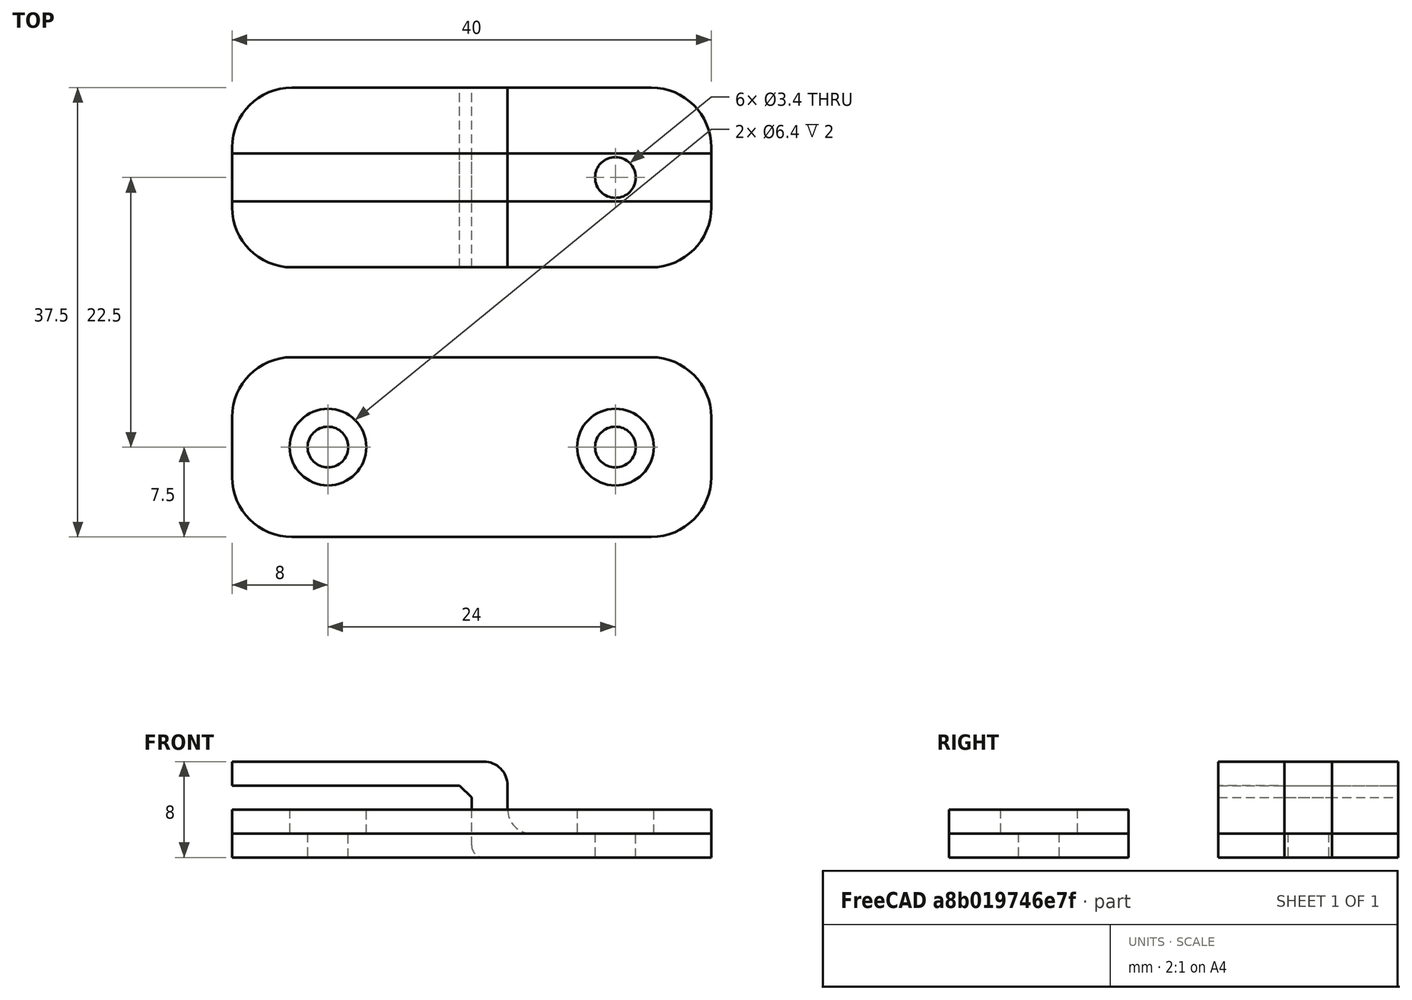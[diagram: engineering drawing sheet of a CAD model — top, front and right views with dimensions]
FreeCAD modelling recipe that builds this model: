
FCSTD DOCUMENT  (FreeCAD 0.20R29177 (Git))
Label: clamp_union_pedales
License: All rights reserved
LicenseURL: http://en.wikipedia.org/wiki/All_rights_reserved
objects: Part::Cut×8, Part::Box×6, Part::Fillet×4, Part::Cylinder×4, Mesh::Feature×4, Part::Feature×3, Part::Chamfer×1, Sketcher::SketchObject×1, PartDesign::Hole×1, PartDesign::Body×1, Part::MultiFuse×1
note: 31 computed .brp shape members not serialized (recipe doc carries the construction recipe); baked Part::Feature solids carry a one-line shape summary decoded from their .brp

FEATURE [Part::Box] Box  label="Cube"
  AttacherType = Attacher::AttachEngine3D
  Height = 8
  Length = 40
  Width = 15
FEATURE [Part::Box] Box001  label="Cube001"
  AttacherType = Attacher::AttachEngine3D
  Height = 6
  Length = 20
  Width = 15
FEATURE [Part::Box] Box002  label="Cube002"
  AttacherType = Attacher::AttachEngine3D
  Height = 6
  Length = 20
  Placement = pos=(23,0,2) rot=(0,0,1;0rad)
  Width = 15
FEATURE [Part::Cut] Cut
  Base = -> Box
  Tool = -> Box002
FEATURE [Part::Cut] Cut001
  Base = -> Cut
  Tool = -> Box001
FEATURE [Part::Fillet] Fillet
  Base = -> Cut001
  Edges = 4 edges r=5: [Edge1,Edge3,Edge5,Edge14]
FEATURE [Part::Fillet] Fillet001
  Base = -> Fillet
  Edges = 2 edges r=2: [Edge9,Edge23]
FEATURE [Part::Chamfer] Chamfer
  Base = -> Fillet001
  Edges = 1 edges r=1: [Edge41]
FEATURE [Part::Fillet] Fillet002
  Base = -> Chamfer
  Edges = 1 edges r=1: [Edge13]
FEATURE [Sketcher::SketchObject] Sketch
  FullyConstrained = false
  MapMode = 5
  Placement = pos=(0,0,2) rot=(0,0,1;0rad)
  Support = -> [Fillet002]
  sketch-geometry (1):
    g0: Circle CenterX=32 CenterY=7.5 CenterZ=0 NormalX=0 NormalY=0 NormalZ=1 AngleXU=0 Radius=2.58429
  constraints (2):
    c: DistanceX(g0) = 32
    c: DistanceY(g-1,g0) = 7.5
FEATURE [PartDesign::Hole] Hole
  CustomThreadClearance = 0
  Depth = 87.7945
  DepthType = 1
  Diameter = 3.4
  DrillForDepth = false
  DrillPoint = 1
  DrillPointAngle = 118
  HoleCutCountersinkAngle = 90
  HoleCutCustomValues = false
  HoleCutDepth = 0
  HoleCutDiameter = 6.1
  HoleCutType = 0
  ModelThread = false
  Profile = -> Sketch
  Tapered = false
  TaperedAngle = 90
  ThreadClass = 0
  ThreadDepth = 87.7945
  ThreadDepthType = 0
  ThreadDirection = 0
  ThreadFit = 0
  ThreadSize = 9
  ThreadType = 1
  Threaded = false
  UseCustomThreadClearance = false
FEATURE [PartDesign::Body] Body  label="clamp"
  Group = -> [Sketch,Hole]
  Origin = -> Origin
  Tip = -> Hole
FEATURE [Part::Box] Box003  label="Cube003"
  AttacherType = Attacher::AttachEngine3D
  Height = 2
  Length = 40
  Width = 15
FEATURE [Part::Fillet] Fillet003
  Base = -> Box003
  Edges = 4 edges r=5: [Edge1,Edge3,Edge5,Edge7]
  Placement = pos=(0,-7.5,0) rot=(0,0,1;0rad)
FEATURE [Part::Cylinder] Cylinder
  Angle = 360
  AttacherType = Attacher::AttachEngine3D
  FirstAngle = 0
  Height = 10
  Placement = pos=(8,0,0) rot=(0,0,1;0rad)
  Radius = 1.7
  SecondAngle = 0
FEATURE [Part::Cylinder] Cylinder001
  Angle = 360
  AttacherType = Attacher::AttachEngine3D
  FirstAngle = 0
  Height = 10
  Placement = pos=(32,0,0) rot=(0,0,1;0rad)
  Radius = 1.7
  SecondAngle = 0
FEATURE [Part::Cut] Cut002
  Base = -> Fillet003
  Tool = -> Cylinder
FEATURE [Part::Cut] Cut003  label="union"
  Base = -> Cut002
  Placement = pos=(0,-15,0) rot=(0,0,1;0rad)
  Tool = -> Cylinder001
FEATURE [Part::Feature] Body001  label="test"
  shape: bbox 40 x 15 x 8 mm, 19 faces (baked)
FEATURE [Part::Box] Box004  label="Cube004"
  AttacherType = Attacher::AttachEngine3D
  Height = 10
  Length = 44
  Width = 5.5
FEATURE [Part::Box] Box005  label="Cube005"
  AttacherType = Attacher::AttachEngine3D
  Height = 10
  Length = 44
  Placement = pos=(0,9.5,0) rot=(0,0,1;0rad)
  Width = 5.5
FEATURE [Part::Cut] Cut004
  Base = -> Body001
  Tool = -> Box004
FEATURE [Part::Cut] Cut005  label="test_clamp"
  Base = -> Cut004
  Tool = -> Box005
FEATURE [Mesh::Feature] Mesh  label="test_clamp (Meshed)"
FEATURE [Mesh::Feature] Mesh001  label="union (Meshed)"
FEATURE [Mesh::Feature] Mesh002  label="clamp (Meshed)"
FEATURE [Part::Feature] Cut003001  label="union001"
  Placement = pos=(0,-15,0) rot=(0,0,1;0rad)
  shape: bbox 40 x 15 x 2 mm, 12 faces (baked)
FEATURE [Part::Feature] Cut003002  label="union002"
  Placement = pos=(0,-15,2) rot=(0,0,1;0rad)
  shape: bbox 40 x 15 x 2 mm, 12 faces (baked)
FEATURE [Part::MultiFuse] Fusion
  Shapes = -> [Cut003001,Cut003002]
FEATURE [Part::Cylinder] Cylinder002
  Angle = 360
  AttacherType = Attacher::AttachEngine3D
  FirstAngle = 0
  Height = 10
  Placement = pos=(32,-15,2) rot=(0,0,1;0rad)
  Radius = 3.2
  SecondAngle = 0
FEATURE [Part::Cylinder] Cylinder003
  Angle = 360
  AttacherType = Attacher::AttachEngine3D
  FirstAngle = 0
  Height = 10
  Placement = pos=(8,-15,2) rot=(0,0,1;0rad)
  Radius = 3.2
  SecondAngle = 0
FEATURE [Part::Cut] Cut003003
  Base = -> Fusion
  Tool = -> Cylinder002
FEATURE [Part::Cut] Cut003004  label="union2"
  Base = -> Cut003003
  Tool = -> Cylinder003
FEATURE [Mesh::Feature] Mesh003  label="union2 (Meshed)"
